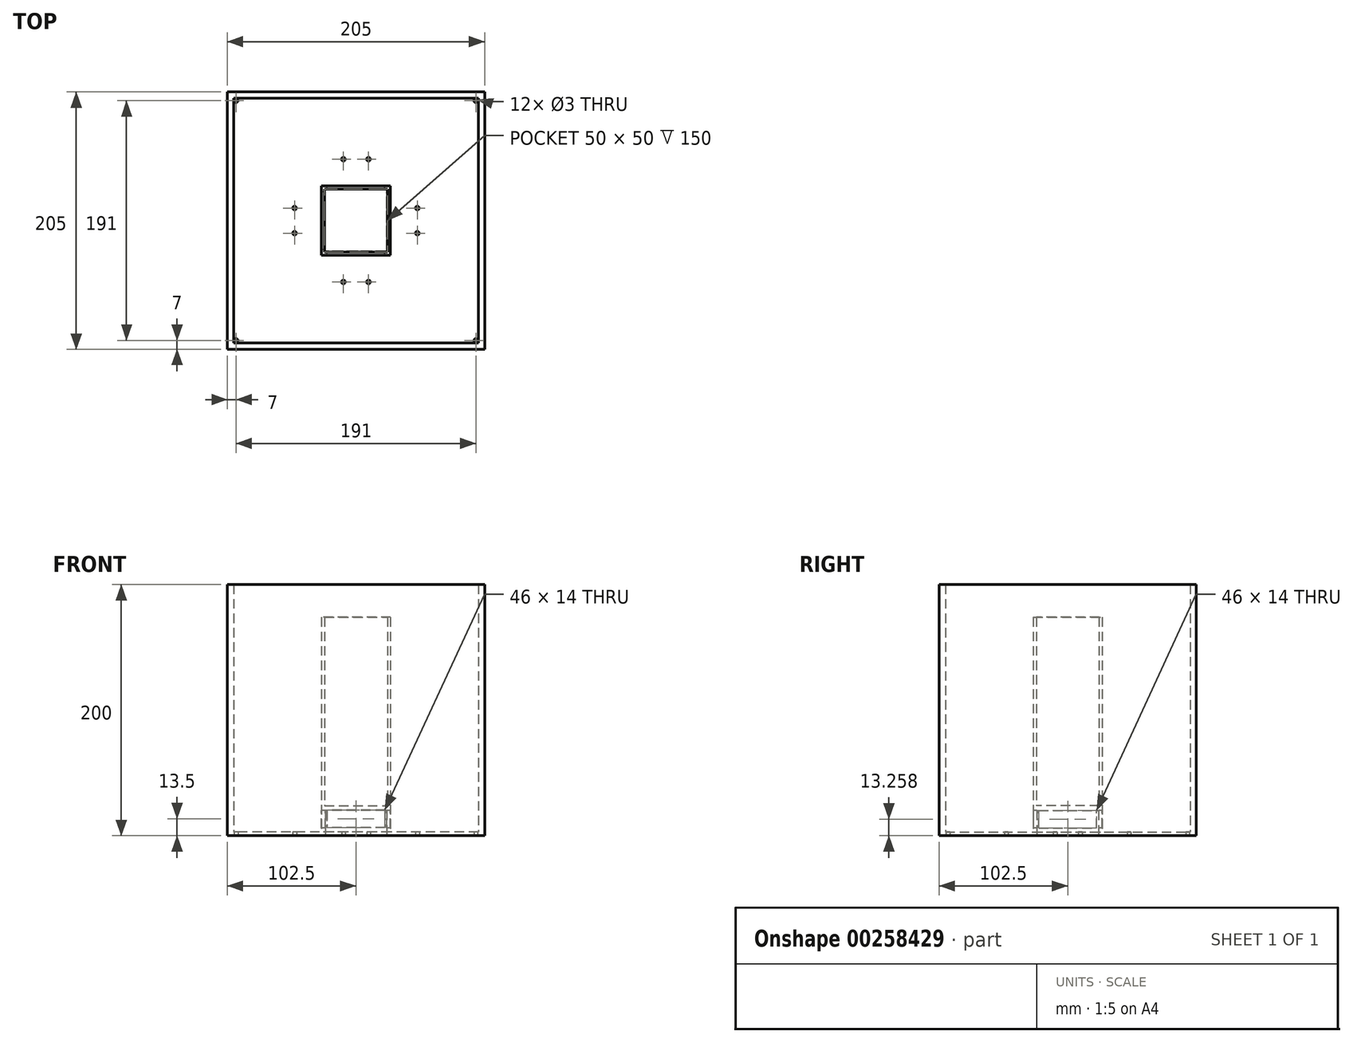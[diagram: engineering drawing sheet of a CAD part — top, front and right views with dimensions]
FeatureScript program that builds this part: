
annotation { "Feature Type Name" : "Feature", "Feature Type Description" : "" }
export const myFeature = defineFeature(function(context is Context, id is Id, definition is map)
    precondition{}
    {
        {
            var Q0;
            Q0=qCreatedBy(makeId("Top.planeOp"),FACE);
            var sketch = newSketch(context, id + "F0", { "sketchPlane" : qUnion([Q0])});
            skLineSegment(sketch, "E0.bottom", {"start": v(97.5, -97.5) * mm, "end": v(-97.5, -97.5) * mm});
            skLineSegment(sketch, "E0.top", {"start": v(97.5, 97.5) * mm, "end": v(-97.5, 97.5) * mm});
            skLineSegment(sketch, "E0.left", {"start": v(97.5, -97.5) * mm, "end": v(97.5, 97.5) * mm});
            skLineSegment(sketch, "E0.right", {"start": v(-97.5, -97.5) * mm, "end": v(-97.5, 97.5) * mm});
            skPoint(sketch, "E0.middle", {"position": v(0, 0) * mm});
            skLineSegment(sketch, "E1", {"start": v(-97.5, 0) * mm, "end": v(97.5, 0) * mm, "construction": true});
            skLineSegment(sketch, "E2", {"start": v(0, -97.5) * mm, "end": v(0, 97.5) * mm, "construction": true});
            skLineSegment(sketch, "E3", {"start": v(-97.5, 97.5) * mm, "end": v(97.5, -97.5) * mm, "construction": true});
            skLineSegment(sketch, "E4", {"start": v(97.5, 97.5) * mm, "end": v(-97.5, -97.5) * mm, "construction": true});
            skCircle(sketch, "E5", {"center": v(10, 48.9) * mm, "radius": 1.5 * mm});
            skCircle(sketch, "E6.MirrorC", {"center": v(48.9, 10) * mm, "radius": 1.5 * mm});
            skCircle(sketch, "E7.MirrorC", {"center": v(-10, 48.9) * mm, "radius": 1.5 * mm});
            skCircle(sketch, "E8.MirrorC", {"center": v(-48.9, 10) * mm, "radius": 1.5 * mm});
            skCircle(sketch, "E9.MirrorC", {"center": v(-48.9, -10) * mm, "radius": 1.5 * mm});
            skCircle(sketch, "E10.MirrorC", {"center": v(-10, -48.9) * mm, "radius": 1.5 * mm});
            skCircle(sketch, "E11.MirrorC", {"center": v(10, -48.9) * mm, "radius": 1.5 * mm});
            skCircle(sketch, "E12.MirrorC", {"center": v(48.9, -10) * mm, "radius": 1.5 * mm});
            skLineSegment(sketch, "E13.0", {"start": v(102.5, -102.5) * mm, "end": v(-102.5, -102.5) * mm});
            skLineSegment(sketch, "E13.1", {"start": v(102.5, -102.5) * mm, "end": v(102.5, 102.5) * mm});
            skLineSegment(sketch, "E13.2", {"start": v(102.5, 102.5) * mm, "end": v(-102.5, 102.5) * mm});
            skLineSegment(sketch, "E13.3", {"start": v(-102.5, -102.5) * mm, "end": v(-102.5, 102.5) * mm});
            skLineSegment(sketch, "E14.bottom", {"start": v(27.5, -27.5) * mm, "end": v(-27.5, -27.5) * mm});
            skLineSegment(sketch, "E14.top", {"start": v(27.5, 27.5) * mm, "end": v(-27.5, 27.5) * mm});
            skLineSegment(sketch, "E14.left", {"start": v(27.5, -27.5) * mm, "end": v(27.5, 27.5) * mm});
            skLineSegment(sketch, "E14.right", {"start": v(-27.5, -27.5) * mm, "end": v(-27.5, 27.5) * mm});
            skLineSegment(sketch, "E15.0", {"start": v(24.5, 24.5) * mm, "end": v(-24.5, 24.5) * mm});
            skLineSegment(sketch, "E15.1", {"start": v(24.5, -24.5) * mm, "end": v(24.5, 24.5) * mm});
            skLineSegment(sketch, "E15.2", {"start": v(24.5, -24.5) * mm, "end": v(-24.5, -24.5) * mm});
            skLineSegment(sketch, "E15.3", {"start": v(-24.5, -24.5) * mm, "end": v(-24.5, 24.5) * mm});
            skCircle(sketch, "E16", {"center": v(-95.5, 95.5) * mm, "radius": 1.5 * mm});
            skCircle(sketch, "E17.MirrorC", {"center": v(95.5, 95.5) * mm, "radius": 1.5 * mm});
            skCircle(sketch, "E18.MirrorC", {"center": v(-95.5, -95.5) * mm, "radius": 1.5 * mm});
            skCircle(sketch, "E19.MirrorC", {"center": v(95.5, -95.5) * mm, "radius": 1.5 * mm});
            skSolve(sketch);
        }
        {
            var Q0;
            Q0=makeQuery(id+"F0.imprint","IMPRINT",FACE,{"disambiguationData":[TD([[makeQuery(id+"F0.imprint","IMPRINT",EDGE,{"derivedFrom":sQuery(id+"F0.wireOp",EDGE,"E0.bottom")}),1.0]])]});
            extrude(context, id + "F1", {"entities" : qUnion([Q0]), "depth" : 200 * mm});
        }
        {
            var Q0;
            Q0=makeQuery(id+"F0.imprint","IMPRINT",FACE,{"disambiguationData":[TD([[makeQuery(id+"F0.imprint","IMPRINT",EDGE,{"derivedFrom":sQuery(id+"F0.wireOp",EDGE,"E0.bottom")}),-1.0]])]});
            extrude(context, id + "F2", {"entities" : qUnion([Q0]), "operationType" : NewBodyOperationType.ADD, "depth" : 3 * mm});
        }
        {
            var Q0;
            Q0=makeQuery(id+"F0.imprint","IMPRINT",FACE,{"disambiguationData":[TD([[makeQuery(id+"F0.imprint","IMPRINT",EDGE,{"derivedFrom":sQuery(id+"F0.wireOp",EDGE,"E14.bottom")}),-1.0]])]});
            extrude(context, id + "F3", {"entities" : qUnion([Q0]), "operationType" : NewBodyOperationType.ADD, "depth" : 24 * mm});
        }
        {
            var Q0;
            Q0=makeQuery(id+"F3.opExtrude","SWEPT_FACE",FACE,{"disambiguationData":[OSD([sQuery(id+"F0.wireOp",EDGE,"E14.right")])]});
            var sketch = newSketch(context, id + "F4", { "sketchPlane" : qUnion([Q0])});
            skLineSegment(sketch, "E20.bottom", {"start": v(23, 6.26) * mm, "end": v(-23, 6.26) * mm});
            skLineSegment(sketch, "E20.top", {"start": v(23, 20.26) * mm, "end": v(-23, 20.26) * mm});
            skLineSegment(sketch, "E20.left", {"start": v(23, 6.26) * mm, "end": v(23, 20.26) * mm});
            skLineSegment(sketch, "E20.right", {"start": v(-23, 6.26) * mm, "end": v(-23, 20.26) * mm});
            skPoint(sketch, "E20.middle", {"position": v(0, 13.26) * mm});
            skSolve(sketch);
        }
        {
            var Q0;
            Q0=makeQuery(id+"F4.imprint","IMPRINT",FACE,{"disambiguationData":[TD([[makeQuery(id+"F4.imprint","IMPRINT",EDGE,{"derivedFrom":sQuery(id+"F4.wireOp",EDGE,"E20.bottom")}),-1.0]])]});
            extrude(context, id + "F5", {"entities" : qUnion([Q0]), "operationType" : NewBodyOperationType.REMOVE, "oppositeDirection" : true, "depth" : 60 * mm});
        }
        {
            var Q0;
            Q0=makeQuery(id+"F3.opExtrude","SWEPT_FACE",FACE,{"disambiguationData":[OSD([sQuery(id+"F0.wireOp",EDGE,"E14.top")])]});
            var sketch = newSketch(context, id + "F6", { "sketchPlane" : qUnion([Q0])});
            skLineSegment(sketch, "E21.bottom", {"start": v(23, 6.5) * mm, "end": v(-23, 6.5) * mm});
            skLineSegment(sketch, "E21.top", {"start": v(23, 20.5) * mm, "end": v(-23, 20.5) * mm});
            skLineSegment(sketch, "E21.left", {"start": v(23, 6.5) * mm, "end": v(23, 20.5) * mm});
            skLineSegment(sketch, "E21.right", {"start": v(-23, 6.5) * mm, "end": v(-23, 20.5) * mm});
            skPoint(sketch, "E21.middle", {"position": v(0, 13.5) * mm});
            skPoint(sketch, "E21.middle.positionSnap0", {"position": v(-27.5, 13.5) * mm});
            skPoint(sketch, "E21.centerSnap0", {"position": v(-27.5, 13.5) * mm});
            skSolve(sketch);
        }
        {
            var Q0;
            Q0=makeQuery(id+"F6.imprint","IMPRINT",FACE,{"disambiguationData":[TD([[makeQuery(id+"F6.imprint","IMPRINT",EDGE,{"derivedFrom":sQuery(id+"F6.wireOp",EDGE,"E21.bottom")}),-1.0]])]});
            extrude(context, id + "F7", {"entities" : qUnion([Q0]), "operationType" : NewBodyOperationType.REMOVE, "oppositeDirection" : true, "depth" : 60 * mm});
        }
        {
            var Q0;
            Q0=makeQuery(id+"F3.opExtrude","CAP_FACE",FACE,{"disambiguationData":[OSD([sQuery(id+"F0.wireOp",EDGE,"E14.bottom"),sQuery(id+"F0.wireOp",EDGE,"E14.top"),sQuery(id+"F0.wireOp",EDGE,"E14.left"),sQuery(id+"F0.wireOp",EDGE,"E14.right"),sQuery(id+"F0.wireOp",EDGE,"E15.0"),sQuery(id+"F0.wireOp",EDGE,"E15.1"),sQuery(id+"F0.wireOp",EDGE,"E15.2"),sQuery(id+"F0.wireOp",EDGE,"E15.3")])],"isStart":false});
            var sketch = newSketch(context, id + "F8", { "sketchPlane" : qUnion([Q0])});
            skLineSegment(sketch, "E22.bottom", {"start": v(-27.5, 27.5) * mm, "end": v(27.5, 27.5) * mm});
            skLineSegment(sketch, "E22.top", {"start": v(-27.5, -27.5) * mm, "end": v(27.5, -27.5) * mm});
            skLineSegment(sketch, "E22.left", {"start": v(-27.5, 27.5) * mm, "end": v(-27.5, -27.5) * mm});
            skLineSegment(sketch, "E22.right", {"start": v(27.5, 27.5) * mm, "end": v(27.5, -27.5) * mm});
            skPoint(sketch, "E22.middle", {"position": v(0, 0) * mm});
            skSolve(sketch);
        }
        {
            var Q0;
            Q0=makeQuery(id+"F8.imprint","IMPRINT",FACE,{"disambiguationData":[TD([[makeQuery(id+"F8.imprint","IMPRINT",EDGE,{"derivedFrom":makeQuery(id+"F3.opExtrude","CAP_EDGE",EDGE,{"disambiguationData":[OSD([sQuery(id+"F0.wireOp",EDGE,"E15.0")])],"isStart":false})}),1.0]])]});
            extrude(context, id + "F9", {"entities" : qUnion([Q0]), "operationType" : NewBodyOperationType.ADD, "oppositeDirection" : true, "depth" : 4 * mm});
        }
        {
            var Q0;
            {var subQ0=sQuery(id+"F0.wireOp",EDGE,"E15.3");var subQ1=sQuery(id+"F0.wireOp",EDGE,"E15.2");var subQ2=sQuery(id+"F0.wireOp",EDGE,"E15.1");var subQ3=sQuery(id+"F0.wireOp",EDGE,"E15.0");Q0=makeQuery(id+"F9.boolean.opBoolean","MERGE",FACE,{"derivedFrom":[makeQuery(id+"F3.opExtrude","CAP_FACE",FACE,{"disambiguationData":[OSD([sQuery(id+"F0.wireOp",EDGE,"E14.bottom"),sQuery(id+"F0.wireOp",EDGE,"E14.top"),sQuery(id+"F0.wireOp",EDGE,"E14.left"),sQuery(id+"F0.wireOp",EDGE,"E14.right"),subQ3,subQ2,subQ1,subQ0])],"isStart":false}),makeQuery(id+"F9.opExtrude","CAP_FACE",FACE,{"disambiguationData":[OSD([subQ3,subQ2,subQ1,subQ0])],"isStart":true})]});}
            var sketch = newSketch(context, id + "F10", { "sketchPlane" : qUnion([Q0])});
            skLineSegment(sketch, "E23.bottom", {"start": v(-25, 25) * mm, "end": v(25, 25) * mm});
            skLineSegment(sketch, "E23.top", {"start": v(-25, -25) * mm, "end": v(25, -25) * mm});
            skLineSegment(sketch, "E23.left", {"start": v(-25, 25) * mm, "end": v(-25, -25) * mm});
            skLineSegment(sketch, "E23.right", {"start": v(25, 25) * mm, "end": v(25, -25) * mm});
            skPoint(sketch, "E23.middle", {"position": v(0, 0) * mm});
            skLineSegment(sketch, "E24.bottom", {"start": v(-27.5, 27.5) * mm, "end": v(27.5, 27.5) * mm});
            skLineSegment(sketch, "E24.top", {"start": v(-27.5, -27.5) * mm, "end": v(27.5, -27.5) * mm});
            skLineSegment(sketch, "E24.left", {"start": v(-27.5, 27.5) * mm, "end": v(-27.5, -27.5) * mm});
            skLineSegment(sketch, "E24.right", {"start": v(27.5, 27.5) * mm, "end": v(27.5, -27.5) * mm});
            skSolve(sketch);
        }
        {
            var Q0;
            Q0=makeQuery(id+"F10.imprint","IMPRINT",FACE,{"disambiguationData":[TD([[makeQuery(id+"F10.imprint","IMPRINT",EDGE,{"derivedFrom":sQuery(id+"F10.wireOp",EDGE,"E23.bottom")}),1.0]])]});
            extrude(context, id + "F11", {"entities" : qUnion([Q0]), "operationType" : NewBodyOperationType.ADD, "depth" : 150 * mm});
        }
    });
